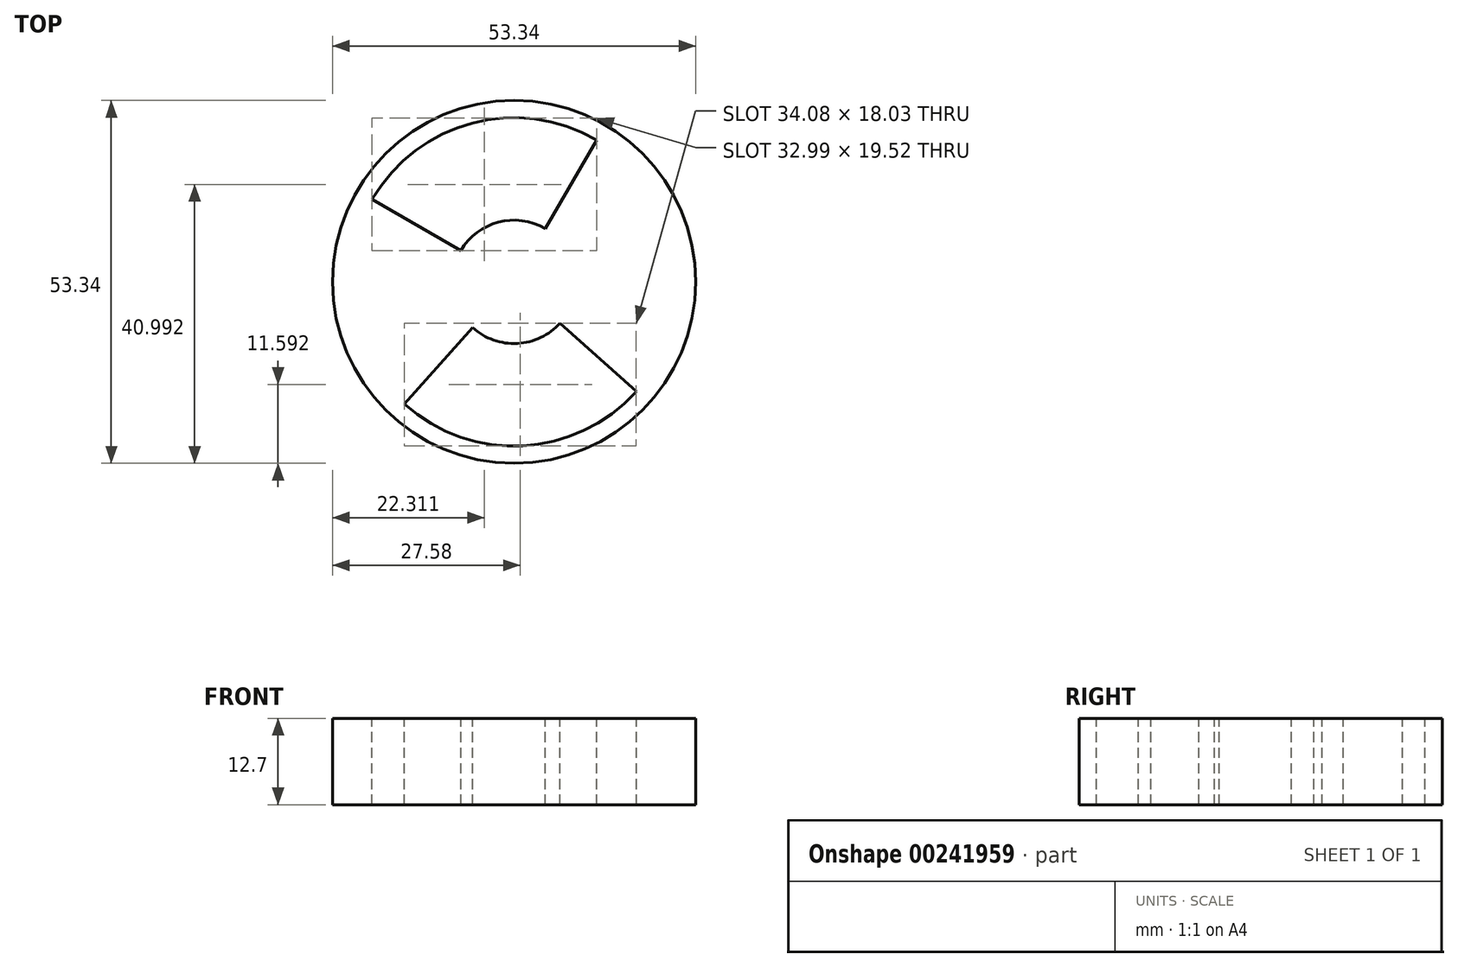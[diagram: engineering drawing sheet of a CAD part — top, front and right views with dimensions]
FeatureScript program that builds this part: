
annotation { "Feature Type Name" : "Feature", "Feature Type Description" : "" }
export const myFeature = defineFeature(function(context is Context, id is Id, definition is map)
    precondition{}
    {
        {
            var Q0;
            Q0=qCreatedBy(makeId("Top.planeOp"),FACE);
            var sketch = newSketch(context, id + "F0", { "sketchPlane" : qUnion([Q0])});
            skCircle(sketch, "E0", {"center": v(0, 0) * mm, "radius": 26.67 * mm});
            skSolve(sketch);
        }
        {
            var Q0;
            Q0=makeQuery(id+"F0.imprint","IMPRINT",FACE,{"disambiguationData":[TD([[makeQuery(id+"F0.imprint","IMPRINT",EDGE,{"derivedFrom":sQuery(id+"F0.wireOp",EDGE,"E0")}),1.0]])]});
            extrude(context, id + "F1", {"entities" : qUnion([Q0]), "depth" : 12.7 * mm});
        }
        {
            var Q0;
            Q0=makeQuery(id+"F1.opExtrude","CAP_FACE",FACE,{"disambiguationData":[OSD([sQuery(id+"F0.wireOp",EDGE,"E0")])],"isStart":false});
            var sketch = newSketch(context, id + "F2", { "sketchPlane" : qUnion([Q0])});
            skCircle(sketch, "E1", {"center": v(0, 0) * mm, "radius": 24.13 * mm});
            skCircle(sketch, "E2", {"center": v(0, 0) * mm, "radius": 9.07 * mm});
            skLineSegment(sketch, "E3", {"start": v(-6.06, -6.74) * mm, "end": v(-16.13, -17.95) * mm});
            skLineSegment(sketch, "E4", {"start": v(6.74, -6.06) * mm, "end": v(17.95, -16.13) * mm});
            skArc(sketch, "E5", {"start": v(-16.13, -17.95) * mm, "mid": v(1.29, -24.14) * mm, "end": v(17.95, -16.13) * mm});
            skArc(sketch, "E6", {"start": v(-6.06, -6.74) * mm, "mid": v(0.48, -9.04) * mm, "end": v(6.74, -6.06) * mm});
            skLineSegment(sketch, "E7", {"start": v(-7.84, 4.56) * mm, "end": v(-20.86, 12.14) * mm});
            skLineSegment(sketch, "E8", {"start": v(4.56, 7.84) * mm, "end": v(12.14, 20.86) * mm});
            skSolve(sketch);
        }
        {
            var Q0;
            {var subQ1=sQuery(id+"F2.wireOp",EDGE,"E3");Q0=makeQuery(id+"F2.imprint","IMPRINT",FACE,{"disambiguationData":[TD([[makeQuery(id+"F2.imprint","IMPRINT",EDGE,{"derivedFrom":subQ1}),1.0]])]});}
            var Q1;
            {var subQ0=sQuery(id+"F2.wireOp",EDGE,"E7");Q1=makeQuery(id+"F2.imprint","IMPRINT",FACE,{"disambiguationData":[TD([[makeQuery(id+"F2.imprint","IMPRINT",EDGE,{"derivedFrom":subQ0}),-1.0]])]});}
            extrude(context, id + "F3", {"entities" : qUnion([Q0, Q1]), "operationType" : NewBodyOperationType.REMOVE, "oppositeDirection" : true, "depth" : 101.6 * mm});
        }
    });
